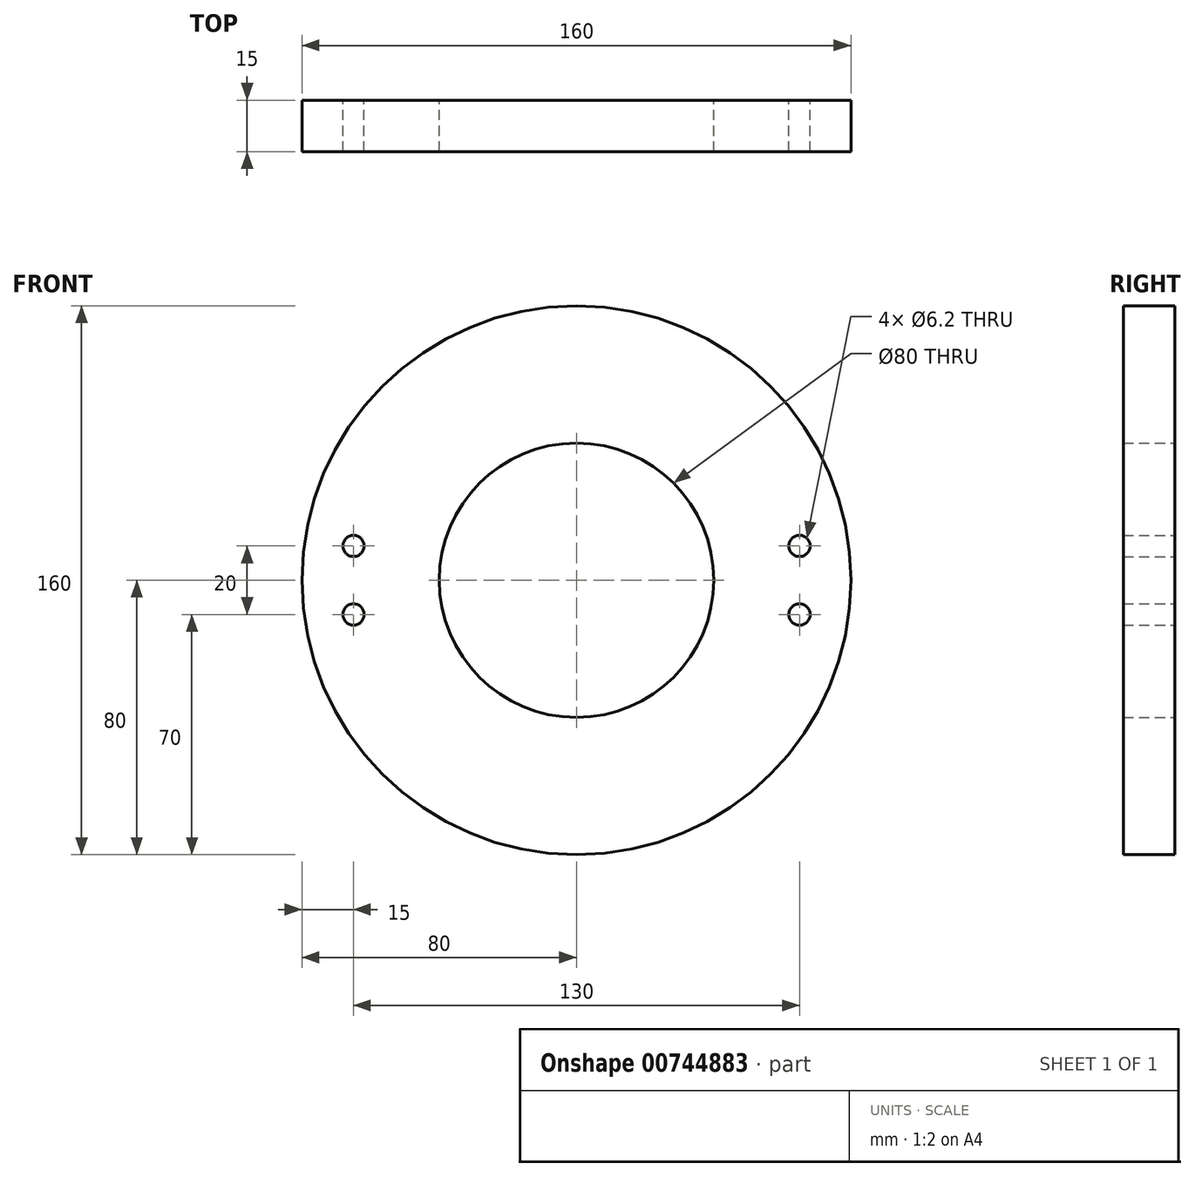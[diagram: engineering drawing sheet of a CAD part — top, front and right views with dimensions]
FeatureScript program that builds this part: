
annotation { "Feature Type Name" : "Feature", "Feature Type Description" : "" }
export const myFeature = defineFeature(function(context is Context, id is Id, definition is map)
    precondition{}
    {
        {
            var Q0;
            Q0=qCreatedBy(makeId("Front.planeOp"),FACE);
            var sketch = newSketch(context, id + "F0", { "sketchPlane" : qUnion([Q0])});
            skCircle(sketch, "E0", {"center": v(0, 0) * mm, "radius": 80 * mm});
            skCircle(sketch, "E1", {"center": v(-65, 10) * mm, "radius": 3.1 * mm});
            skCircle(sketch, "E2.MirrorC", {"center": v(-65, -10) * mm, "radius": 3.1 * mm});
            skCircle(sketch, "E3.MirrorC", {"center": v(65, -10) * mm, "radius": 3.1 * mm});
            skCircle(sketch, "E4.MirrorC", {"center": v(65, 10) * mm, "radius": 3.1 * mm});
            skCircle(sketch, "E5", {"center": v(0, 0) * mm, "radius": 40 * mm});
            skSolve(sketch);
        }
        {
            var Q0;
            Q0 = qSketchRegion(id + "F0", true);
            extrude(context, id + "F1", {"entities" : qUnion([Q0]), "depth" : 15 * mm, "offsetDistance" : 25 * mm});
        }
    });
